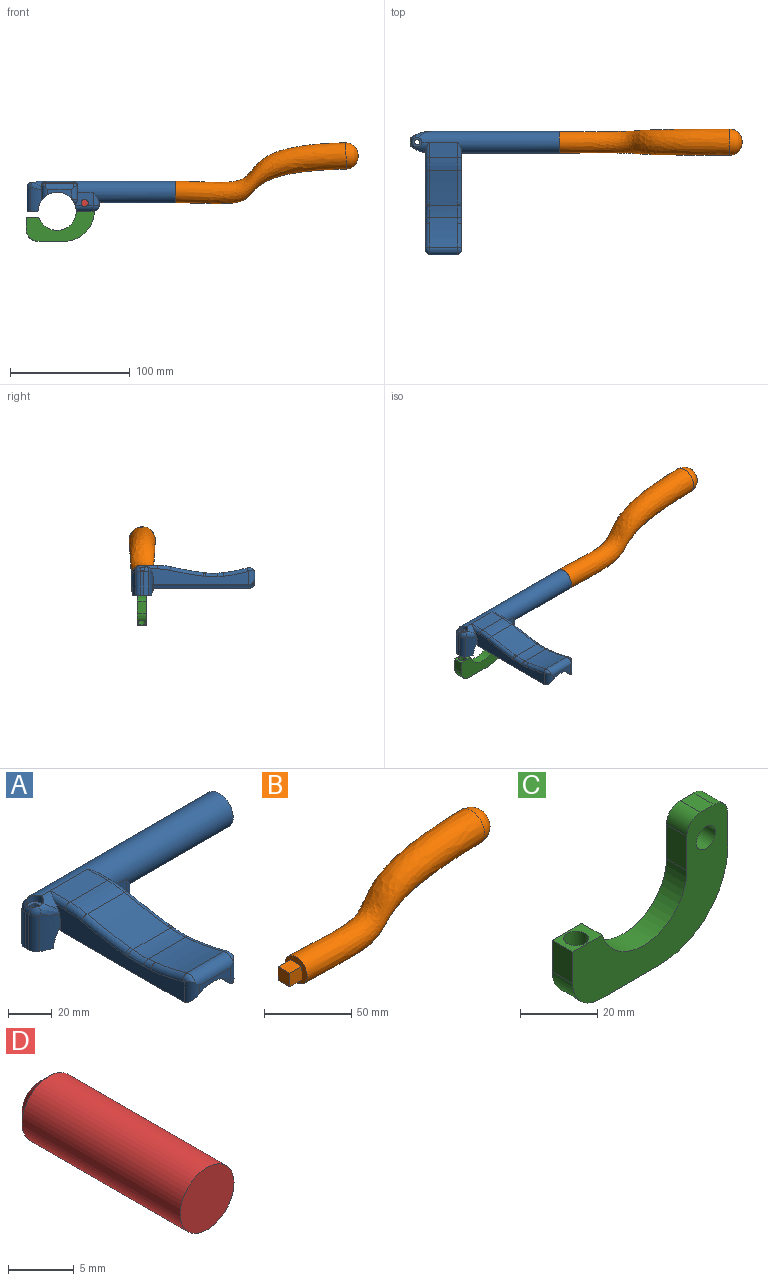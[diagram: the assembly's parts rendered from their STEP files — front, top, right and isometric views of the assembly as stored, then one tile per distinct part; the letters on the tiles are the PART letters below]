
ASSEMBLY  parts=4 mates=3
PART A: 79 faces, bbox 123.6x103.1x25.4 mm
  f0: plane 15.46x10mm, normal (0,1,0), area 57.1mm2, adj f49,f50,f73,f75
  f1: plane 12.02x7.06mm, normal (0,1,0), area 27.4mm2, adj f48,f49,f73
  f2: plane 24x12.66mm, normal (0,0,1), area 303.8mm2, adj f4,f55,f57,f65
  f3: plane 28.74x11mm, normal (0,-1,0), area 181.8mm2, adj f4,f10,f30,f41,f43,f49,f50
  f4: cylinder r=9mm len=117.38mm, axis (-1,0,0), area 4561.1mm2, adj f2,f3,f5,f7,f11,f13,f14,f24
  f5: cylinder r=9mm len=8.88mm, axis (-1,0,0), area 46.6mm2, adj f4,f14,f35,f48,f65
  f6: plane 14.05x0.5mm, normal (0,0,-1), area 7mm2, adj f10,f25,f31,f43
  f7: plane 18x18mm, normal (1,0,0), area 173.5mm2, adj f4,f19,f20,f21,f22
  f8: plane 20x2.31mm, normal (-1,0,0), area 46.1mm2, adj f9,f32,f33,f37
  f9: plane 16.08x9.05mm, normal (0,0,-1), area 95.8mm2, adj f8,f10,f16,f17,f18,f32,f33
  f10: cylinder r=15.95mm len=31.9mm, axis (0,1,0), area 666.9mm2, adj f3,f6,f9,f12,f13,f17,f18,f25
  f11: plane 2.94x0.5mm, normal (1,0,0), area 1.4mm2, adj f4,f25,f31,f41
  f12: plane 7.69x2.7mm, normal (0,-1,0), area 7.5mm2, adj f10,f34,f49
  f13: plane 38.97x11.03mm, normal (0,1,0), area 192.3mm2, adj f4,f10,f29,f40,f44,f45,f46
  f14: cylinder r=4mm len=8mm, axis (0,0,1), area 76.5mm2, adj f4,f5,f15,f35,f36,f37,f38,f39
  f15: plane 8x8mm, normal (0,0,1), area 34.4mm2, adj f14,f16
  f16: cylinder r=2.25mm len=21mm, axis (0,0,1), area 296.9mm2, adj f9,f15
  f17: cylinder r=30mm len=19.83mm, axis (0,0,1), area 183.4mm2, adj f9,f10,f32,f34,f35
  f18: cylinder r=30mm len=19.83mm, axis (0,0,1), area 183.4mm2, adj f9,f10,f33,f39,f40
  f19: plane 20x9mm, normal (0,0,-1), area 180mm2, adj f7,f20,f22,f23
  f20: plane 20x9mm, normal (0,1,0), area 180mm2, adj f7,f19,f21,f23
  f21: plane 20x9mm, normal (0,0,1), area 180mm2, adj f7,f20,f22,f23
  f22: plane 20x9mm, normal (0,-1,0), area 180mm2, adj f7,f19,f21,f23
  f23: plane 9x9mm, normal (1,0,0), area 81mm2, adj f19,f20,f21,f22
  f24: plane 13x8mm, normal (-1,0,0), area 101.4mm2, adj f4,f25,f26,f28
  f25: plane 40x20mm, normal (0,1,0), area 519.8mm2, adj f4,f6,f10,f11,f24,f27,f28,f30
  f26: plane 40x20mm, normal (0,-1,0), area 517.8mm2, adj f4,f10,f24,f27,f28,f29,f44,f45
  f27: plane 8x4.08mm, normal (1,0,0), area 32.7mm2, adj f10,f25,f26,f28
  f28: plane 40x8mm, normal (0,0,-1), area 320mm2, adj f24,f25,f26,f27
  f29: cylinder r=3mm len=6mm, axis (0,-1,0), area 84.8mm2, adj f13,f26,f46
  f30: cylinder r=3mm len=6mm, axis (0,-1,0), area 103.7mm2, adj f3,f25,f43
  f31: cylinder r=5mm len=5mm, axis (0,1,0), area 3.9mm2, adj f6,f11,f25,f42
  f32: cylinder r=5mm len=19.83mm, axis (0,0,1), area 107.9mm2, adj f8,f9,f17,f36
  f33: cylinder r=5mm len=19.83mm, axis (0,0,1), area 107.9mm2, adj f8,f9,f18,f38
  f34: cylinder r=5mm len=2.87mm, axis (0,0,1), area 0.3mm2, adj f10,f12,f17,f35,f47
  f35: bspline ~13.72x8.76mm, area 48.1mm2, adj f5,f14,f17,f34,f36,f47
  f36: sphere r=5mm, area 19.5mm2, adj f14,f32,f35,f37
  f37: torus R=4mm, axis (-1,0,0), area 11.8mm2, adj f8,f14,f36,f38
  f38: sphere r=5mm, area 19.5mm2, adj f14,f33,f37,f39
  f39: bspline ~14.79x8.97mm, area 48.1mm2, adj f4,f14,f18,f38,f40
  f40: cylinder r=5mm len=2.87mm, axis (0,0,1), area 0.3mm2, adj f10,f13,f18,f39
  f41: cylinder r=5mm len=11mm, axis (0,0,-1), area 54.7mm2, adj f3,f4,f11,f42
  f42: sphere r=5mm, area 25mm2, adj f31,f41,f43
  f43: cylinder r=5mm len=14.85mm, axis (-1,0,0), area 110.4mm2, adj f3,f6,f10,f30,f42
  f44: cylinder r=5mm len=11mm, axis (0,0,1), area 52.2mm2, adj f4,f13,f26,f45
  f45: torus R=0.03mm, axis (0,1,0), area 35.6mm2, adj f13,f26,f44,f46
  f46: cylinder r=5mm len=14.85mm, axis (1,0,0), area 103.2mm2, adj f10,f13,f26,f29,f45
  f47: cylinder r=9mm len=4.11mm, axis (-1,0,0), area 9.5mm2, adj f34,f35,f48,f49
  f48: plane 82.3x13.18mm, normal (-1,0,0), area 750.1mm2, adj f1,f5,f47,f49,f65,f66,f67,f68
  f49: plane 30.1x0.5mm, normal (0,0,-1), area 12mm2, adj f0,f1,f3,f10,f12,f47,f48,f50
  f50: plane 82.32x12.21mm, normal (1,0,0), area 671.4mm2, adj f0,f3,f4,f49,f57,f58,f59,f60
  f51: plane 20x7.31mm, normal (0,-1,0), area 68.2mm2, adj f56,f73,f76,f78
  f52: cylinder r=308.82mm len=29.52mm, axis (-1,0,0), area 719.2mm2, adj f54,f55,f59,f60,f67,f68
  f53: cylinder r=118.83mm len=24.7mm, axis (-1,0,0), area 603.8mm2, adj f54,f56,f62,f63,f70,f71
  f54: cylinder r=50mm len=24.07mm, axis (1,0,0), area 236.2mm2, adj f52,f53,f61,f69
  f55: cylinder r=50mm len=24mm, axis (-1,0,0), area 264mm2, adj f2,f52,f58,f66
  f56: cylinder r=5mm len=24mm, axis (-1,0,0), area 218.6mm2, adj f51,f53,f64,f72,f76,f78
  f57: cylinder r=3mm len=12.66mm, axis (0,-1,0), area 43.8mm2, adj f2,f4,f50,f58
  f58: torus R=47mm, axis (-1,0,0), area 50.7mm2, adj f50,f55,f57,f59
  f59: torus R=311.82mm, axis (-1,0,0), area 134.5mm2, adj f50,f52,f58,f60
  f60: bspline ~11.41x3.45mm, area 7.1mm2, adj f50,f52,f59,f61
  f61: bspline ~14.24x3.05mm, area 42.3mm2, adj f50,f54,f60,f62
  f62: bspline ~8.4x3.23mm, area 21.1mm2, adj f50,f53,f61,f63
  f63: torus R=121.83mm, axis (-1,0,0), area 97.2mm2, adj f50,f53,f62,f64
  f64: torus R=2mm, axis (-1,0,0), area 19.6mm2, adj f50,f56,f63,f76
  f65: cylinder r=3mm len=12.66mm, axis (0,1,0), area 43.8mm2, adj f2,f5,f48,f66
  f66: torus R=47mm, axis (-1,0,0), area 50.7mm2, adj f48,f55,f65,f67
  f67: torus R=311.82mm, axis (-1,0,0), area 134.5mm2, adj f48,f52,f66,f68
  f68: bspline ~11.41x3.45mm, area 7.1mm2, adj f48,f52,f67,f69
  f69: bspline ~13.45x3.08mm, area 42.3mm2, adj f48,f54,f68,f70
  f70: bspline ~8.4x3.23mm, area 21.1mm2, adj f48,f53,f69,f71
  f71: torus R=121.83mm, axis (-1,0,0), area 97.2mm2, adj f48,f53,f70,f72
  f72: torus R=2mm, axis (-1,0,0), area 19.6mm2, adj f48,f56,f71,f78
  f73: cylinder r=15.95mm len=84.6mm, axis (0,1,0), area 2921.5mm2, adj f0,f1,f48,f51,f74,f75,f76,f77
  f74: plane 2.52x0.05mm, normal (0,-1,0), area 0.1mm2, adj f49,f73
  f75: cylinder r=5mm len=79.6mm, axis (0,1,0), area 359.2mm2, adj f0,f50,f73,f77
  f76: cylinder r=5mm len=11.3mm, axis (0,0,1), area 82.4mm2, adj f50,f51,f56,f64,f73,f77
  f77: sphere r=5mm, area 13.4mm2, adj f73,f75,f76
  f78: cylinder r=5mm len=11.29mm, axis (0,0,-1), area 67.8mm2, adj f48,f51,f56,f72,f73
PART B: 9 faces, bbox 162.4x22x51.1 mm
  f0: plane 18x18mm, normal (-1,0,0), area 164.2mm2, adj f2,f4,f5,f6,f7
  f1: plane 1.99x1.99mm, normal (1,0,0), area 3.1mm2, adj f3
  f2: bspline ~142.57x50.84mm, area 9159.3mm2, adj f0,f3
  f3: bspline ~22.19x22.02mm, area 726.4mm2, adj f1,f2
  f4: plane 10x9.5mm, normal (0,0,1), area 95mm2, adj f0,f5,f7,f8
  f5: plane 10x9.5mm, normal (0,1,0), area 95mm2, adj f0,f4,f6,f8
  f6: plane 10x9.5mm, normal (0,0,-1), area 95mm2, adj f0,f5,f7,f8
  f7: plane 10x9.5mm, normal (0,-1,0), area 95mm2, adj f0,f4,f6,f8
  f8: plane 9.5x9.5mm, normal (-1,0,0), area 90.2mm2, adj f4,f5,f6,f7
PART C: 15 faces, bbox 56.9x7.5x41 mm
  f0: cylinder r=15.95mm len=31.1mm, axis (0,1,0), area 337.7mm2, adj f5,f7,f8,f9
  f1: plane 10x7.5mm, normal (-1,0,0), area 75mm2, adj f7,f8,f9,f14
  f2: plane 21.9x7.5mm, normal (0,0,-1), area 164.2mm2, adj f7,f8,f13,f14
  f3: plane 10.95x7.5mm, normal (1,0,0), area 82.1mm2, adj f7,f8,f11,f13
  f4: plane 7.5x5mm, normal (0,0,1), area 37.5mm2, adj f7,f8,f11,f12
  f5: plane 10.95x7.5mm, normal (-1,0,0), area 82.1mm2, adj f0,f7,f8,f12
  f6: cylinder r=3.5mm len=7.5mm, axis (0,1,0), area 164.9mm2, adj f7,f8
  f7: plane 56.9x40.95mm, normal (0,-1,0), area 1006mm2, adj f0,f1,f2,f3,f4,f5,f6,f9
  f8: plane 56.9x40.95mm, normal (0,1,0), area 1006mm2, adj f0,f1,f2,f3,f4,f5,f6,f9
  f9: plane 10.8x7.5mm, normal (0,0,1), area 48.4mm2, adj f0,f1,f7,f8,f10
  f10: cylinder r=3.23mm len=19.84mm, axis (0,0,1), area 369.3mm2, adj f9,f14
  f11: cylinder r=5mm len=7.5mm, axis (0,1,0), area 58.9mm2, adj f3,f4,f7,f8
  f12: cylinder r=5mm len=7.5mm, axis (0,1,0), area 58.9mm2, adj f4,f5,f7,f8
  f13: cylinder r=25mm len=25mm, axis (0,1,0), area 294.5mm2, adj f2,f3,f7,f8
  f14: cylinder r=10mm len=10mm, axis (0,1,0), area 78.5mm2, adj f1,f2,f7,f8,f10
PART D: 4 faces, bbox 5.8x18x5.8 mm
  f0: cylinder r=2.9mm len=17mm, axis (0,1,0), area 309.8mm2, adj f1,f3
  f1: plane 5.8x5.8mm, normal (0,-1,0), area 26.4mm2, adj f0
  f2: plane 3.8x3.8mm, normal (0,1,0), area 11.3mm2, adj f3
  f3: cone r=2.9mm half-angle=45deg, axis (0,-1,0), area 21.3mm2, adj f0,f2
PLACE A t=(-77.03,78.94,-76.48)mm
PLACE B t=(46.47,69.94,-60.23)mm
PLACE C t=(-52.03,73.94,-76.48)mm
PLACE D t=(-29.08,78.94,-69.48)mm
MATE fastened D.f0 <-> A.f29  axis (0,-1,0) through (-29.08,60.94,-69.48)mm
MATE revolute C.f6 <-> A.f29  axis (0,1,0) through (-29.08,66.44,-69.48)mm
MATE fastened A.f21 <-> B.f6  axis (0,0,1) through (46.47,69.94,-64.98)mm
